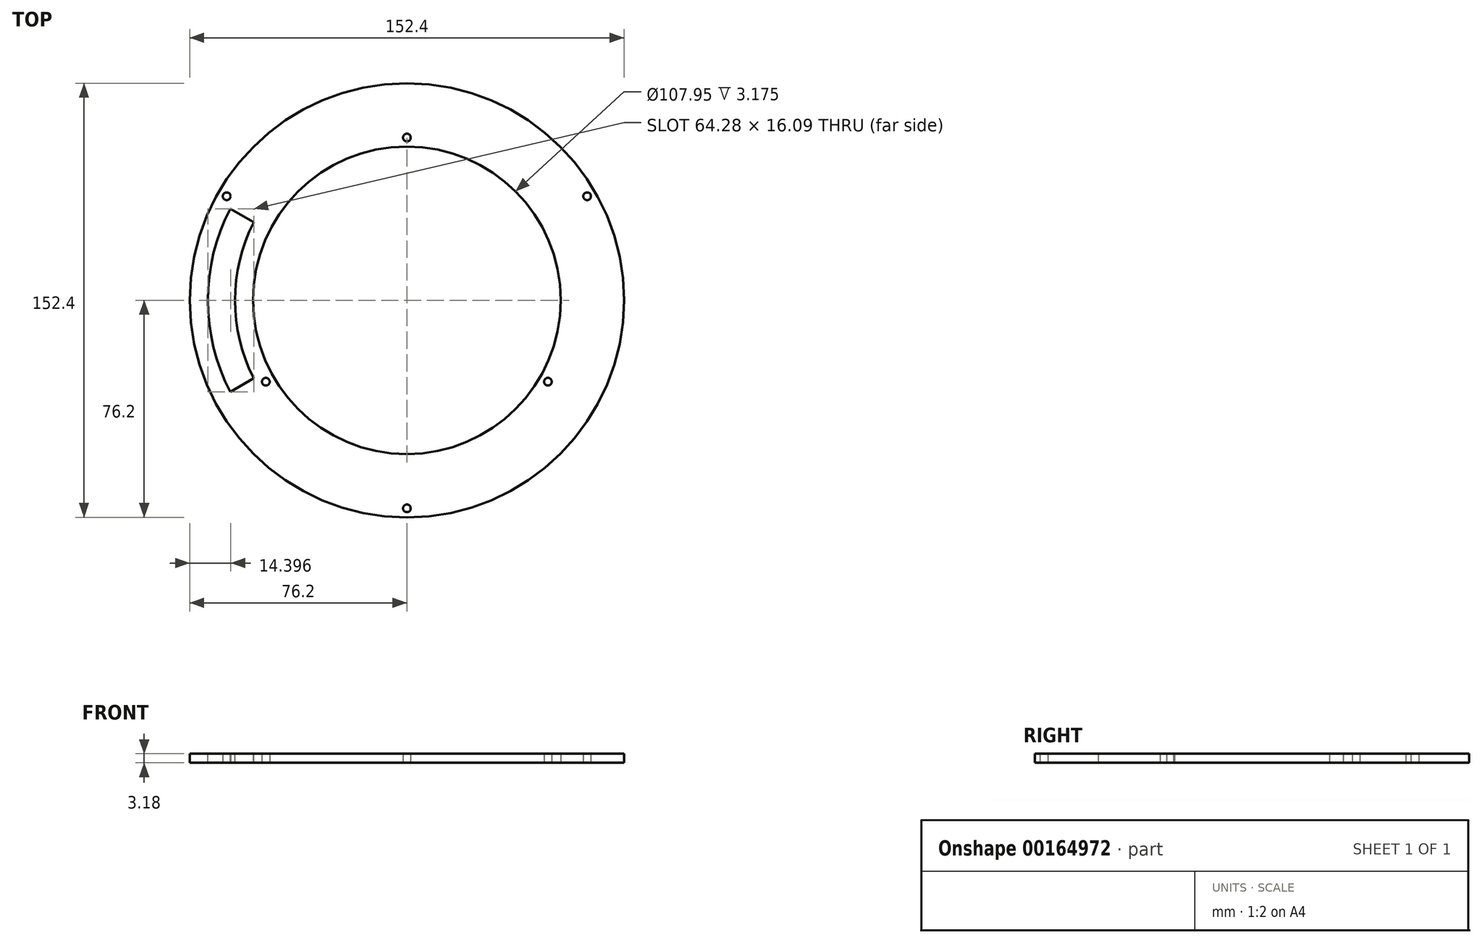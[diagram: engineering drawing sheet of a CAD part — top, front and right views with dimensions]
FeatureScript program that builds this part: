
annotation { "Feature Type Name" : "Feature", "Feature Type Description" : "" }
export const myFeature = defineFeature(function(context is Context, id is Id, definition is map)
    precondition{}
    {
        {
            var Q0;
            Q0=qCreatedBy(makeId("Top.planeOp"),FACE);
            var sketch = newSketch(context, id + "F0", { "sketchPlane" : qUnion([Q0])});
            skCircle(sketch, "E0", {"center": v(0, 0) * mm, "radius": 53.98 * mm});
            skCircle(sketch, "E1", {"center": v(0, 0) * mm, "radius": 76.2 * mm});
            skCircle(sketch, "E2.cCircle", {"center": v(0, 0) * mm, "radius": 36.51 * mm, "construction": true});
            skLineSegment(sketch, "E2.0", {"start": v(-63.24, 36.51) * mm, "end": v(63.24, 36.51) * mm, "construction": true});
            skLineSegment(sketch, "E2.1", {"start": v(63.24, 36.51) * mm, "end": v(0, -73.03) * mm, "construction": true});
            skLineSegment(sketch, "E2.2", {"start": v(0, -73.03) * mm, "end": v(-63.24, 36.51) * mm, "construction": true});
            skPoint(sketch, "E2.0.midPoint", {"position": v(0, 36.51) * mm});
            skCircle(sketch, "E3", {"center": v(0, -73.03) * mm, "radius": 3.18 * mm, "construction": true});
            skCircle(sketch, "E4", {"center": v(0, -73.03) * mm, "radius": 1.35 * mm});
            skCircle(sketch, "E5", {"center": v(63.24, 36.51) * mm, "radius": 1.35 * mm});
            skCircle(sketch, "E6", {"center": v(-63.24, 36.51) * mm, "radius": 1.35 * mm});
            skCircle(sketch, "E7.cCircle", {"center": v(0, 0) * mm, "radius": 28.57 * mm, "construction": true});
            skLineSegment(sketch, "E7.0", {"start": v(49.5, -28.57) * mm, "end": v(-49.5, -28.57) * mm, "construction": true});
            skLineSegment(sketch, "E7.1", {"start": v(-49.5, -28.58) * mm, "end": v(0, 57.15) * mm, "construction": true});
            skLineSegment(sketch, "E7.2", {"start": v(0, 57.15) * mm, "end": v(49.5, -28.58) * mm, "construction": true});
            skCircle(sketch, "E8", {"center": v(0, 57.15) * mm, "radius": 3.18 * mm, "construction": true});
            skCircle(sketch, "E9", {"center": v(0, 57.15) * mm, "radius": 1.35 * mm});
            skCircle(sketch, "E10", {"center": v(-49.5, -28.57) * mm, "radius": 1.35 * mm});
            skCircle(sketch, "E11", {"center": v(49.5, -28.57) * mm, "radius": 1.35 * mm});
            skSolve(sketch);
        }
        {
            var Q0;
            Q0=qSketchRegion(id+"F0",true);
            extrude(context, id + "F1", {"entities" : qUnion([Q0]), "depth" : 3.17 * mm});
        }
        {
            var Q0;
            Q0=makeQuery(id+"F1.opExtrude","CAP_FACE",FACE,{"disambiguationData":[OSD([sQuery(id+"F0.wireOp",EDGE,"E0"),sQuery(id+"F0.wireOp",EDGE,"E1"),sQuery(id+"F0.wireOp",EDGE,"E4"),sQuery(id+"F0.wireOp",EDGE,"E5"),sQuery(id+"F0.wireOp",EDGE,"E6"),sQuery(id+"F0.wireOp",EDGE,"E9"),sQuery(id+"F0.wireOp",EDGE,"E10"),sQuery(id+"F0.wireOp",EDGE,"E11")])],"isStart":false});
            var sketch = newSketch(context, id + "F2", { "sketchPlane" : qUnion([Q0])});
            skLineSegment(sketch, "E12", {"start": v(-49.5, -28.58) * mm, "end": v(0, 0) * mm, "construction": true});
            skLineSegment(sketch, "E13", {"start": v(-49.5, -28.58) * mm, "end": v(-51.08, -25.83) * mm, "construction": true});
            skLineSegment(sketch, "E14", {"start": v(0, 0) * mm, "end": v(-63.24, 36.51) * mm, "construction": true});
            skLineSegment(sketch, "E15", {"start": v(-63.24, 36.51) * mm, "end": v(-64.83, 33.76) * mm, "construction": true});
            skArc(sketch, "E16", {"start": v(-53.76, 27.37) * mm, "mid": v(-60.33, 0) * mm, "end": v(-53.76, -27.37) * mm});
            skArc(sketch, "E17", {"start": v(-62.02, 32.14) * mm, "mid": v(-69.85, 0) * mm, "end": v(-62.02, -32.14) * mm});
            skLineSegment(sketch, "E18", {"start": v(-62.02, 32.14) * mm, "end": v(-53.76, 27.37) * mm});
            skLineSegment(sketch, "E19", {"start": v(-62.02, -32.14) * mm, "end": v(-53.76, -27.37) * mm});
            skLineSegment(sketch, "E20", {"start": v(-62.02, 32.14) * mm, "end": v(-64.83, 33.76) * mm, "construction": true});
            skLineSegment(sketch, "E21", {"start": v(-51.08, -25.83) * mm, "end": v(-53.76, -27.37) * mm, "construction": true});
            skSolve(sketch);
        }
        {
            var Q0;
            Q0 = qSketchRegion(id + "F2", true);
            var Q1;
            Q1=makeQuery(id+"F1.opExtrude","CAP_FACE",FACE,{"disambiguationData":[OSD([sQuery(id+"F0.wireOp",EDGE,"E0"),sQuery(id+"F0.wireOp",EDGE,"E1"),sQuery(id+"F0.wireOp",EDGE,"E4"),sQuery(id+"F0.wireOp",EDGE,"E5"),sQuery(id+"F0.wireOp",EDGE,"E6"),sQuery(id+"F0.wireOp",EDGE,"E9"),sQuery(id+"F0.wireOp",EDGE,"E10"),sQuery(id+"F0.wireOp",EDGE,"E11")])],"isStart":true});
            extrude(context, id + "F3", {"entities" : qUnion([Q0]), "operationType" : NewBodyOperationType.REMOVE, "endBound" : BoundingType.UP_TO_SURFACE, "oppositeDirection" : true, "endBoundEntityFace" : qUnion([Q1]), "depth" : 25.4 * mm});
        }
    });
